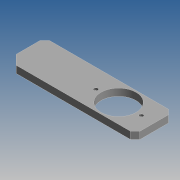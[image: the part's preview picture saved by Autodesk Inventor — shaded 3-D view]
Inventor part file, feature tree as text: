
AUTODESK INVENTOR PART (.ipt)
format: ipt  version: 2015 SP1 (Build 190203100, 203)  size: 217,088 bytes
history: native  units: mm
features: sketch x3, hole x2, chamfer x2, extrude x1
ambient origin geometry x8: Origin, YZ Plane, XZ Plane, XY Plane, X Axis, Y Axis, Z Axis, Center Point
bodies: Solid1 (feature_tree)
feature tree (8):
  extrude  "Extrusion1"  Depth=16.0mm
  hole  "Hole1"  [1 undecoded]
  chamfer  "Chamfer2"  Distance=2.0mm Angle=45.0deg
  chamfer  "Chamfer3"  Distance=4.0mm Angle=45.0deg
  hole  "Hole2"  [1 undecoded]
  sketch  "Sketch1"  dims[d0=54.0mm d1=16.0mm]
  sketch  "Sketch2"  dims[d2=3.0mm d3=0.0mm d4=12.0mm]
  sketch  "Sketch3"  dims[d5=14.7mm d6=6.0mm d7=4.0mm d8=2.0mm d9=90.0deg d10=8.0mm d11=20.594885mm d15=2.0mm d16=2.0mm d17=45.0deg d18=4.0mm d19=2.0mm d20=45.0deg d21=9.53mm d22=9.53mm d23=1.567mm d24=4.0mm d25=4.0mm d26=2.0mm d27=90.0deg d28=6.3mm d29=20.594885mm]
note: 2 required parameter values undecoded (feature->parameter linkage not recoverable at this tier; creation-order binding heuristic only, values carry confidence <= 0.55)
